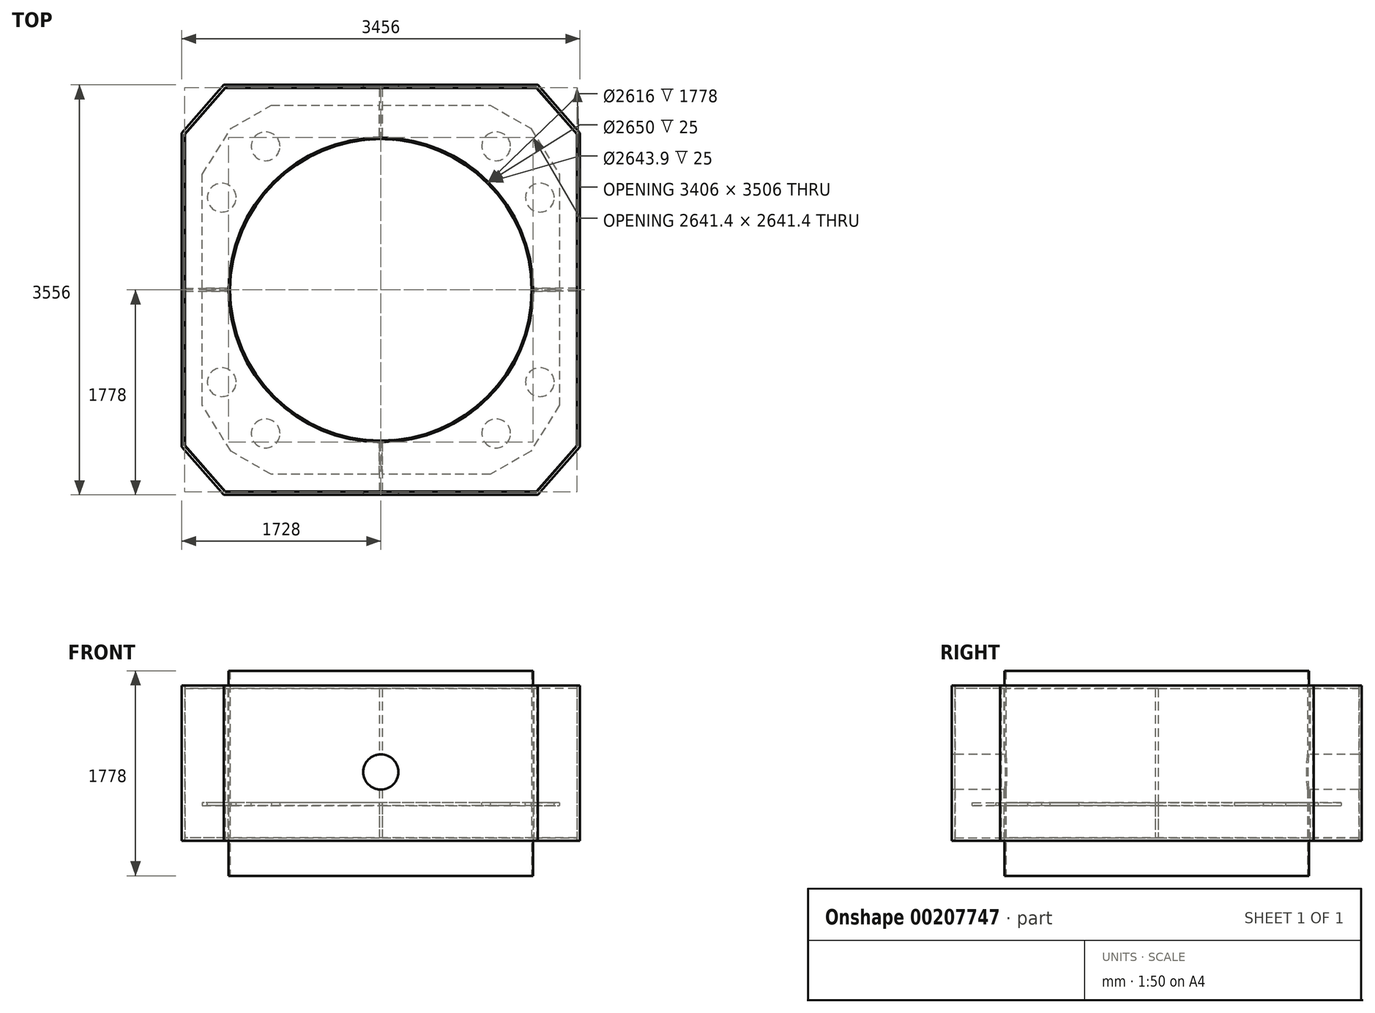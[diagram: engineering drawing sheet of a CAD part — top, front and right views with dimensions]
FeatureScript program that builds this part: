
annotation { "Feature Type Name" : "Feature", "Feature Type Description" : "" }
export const myFeature = defineFeature(function(context is Context, id is Id, definition is map)
    precondition{}
    {
        {
            var Q0;
            Q0=qCreatedBy(makeId("Front.planeOp"),FACE);
            var sketch = newSketch(context, id + "F0", { "sketchPlane" : qUnion([Q0])});
            skLineSegment(sketch, "E0", {"start": v(0, 0) * mm, "end": v(0, 90.62) * mm, "construction": true});
            skLineSegment(sketch, "E1.bottom", {"start": v(1308, 1778) * mm, "end": v(1320.7, 1778) * mm});
            skLineSegment(sketch, "E1.top", {"start": v(1308, 0) * mm, "end": v(1320.7, 0) * mm});
            skLineSegment(sketch, "E1.left", {"start": v(1308, 1778) * mm, "end": v(1308, 0) * mm});
            skLineSegment(sketch, "E1.right", {"start": v(1320.7, 1778) * mm, "end": v(1320.7, 0) * mm});
            skSolve(sketch);
        }
        {
            var Q0;
            Q0 = qSketchRegion(id + "F0", true);
            var Q1;
            Q1=sQuery(id+"F0.wireOp",EDGE,"E0");
            revolve(context, id + "F1", {"surfaceOperationType" : NewSurfaceOperationType.NEW, "entities" : qUnion([Q0]), "axis" : qUnion([Q1]), "revolveType" : RevolveType.FULL});
        }
        {
            var Q0;
            Q0=qCreatedBy(makeId("Top.planeOp"),FACE);
            cPlane(context, id + "F2", {"entities" : qUnion([Q0]), "cplaneType" : CPlaneType.OFFSET, "offset" : 304 * mm, "width" : 150 * mm, "height" : 150 * mm});
        }
        {
            var Q0;
            Q0=qCreatedBy(id+"F2.planeOp",FACE);
            var sketch = newSketch(context, id + "F3", { "sketchPlane" : qUnion([Q0])});
            skLineSegment(sketch, "E2.bottom", {"start": v(-1700, -1750) * mm, "end": v(1700, -1750) * mm});
            skLineSegment(sketch, "E2.top", {"start": v(-1700, 1750) * mm, "end": v(1700, 1750) * mm});
            skLineSegment(sketch, "E2.left", {"start": v(-1700, -1750) * mm, "end": v(-1700, 1750) * mm});
            skLineSegment(sketch, "E2.right", {"start": v(1700, -1750) * mm, "end": v(1700, 1750) * mm});
            skCircle(sketch, "E3", {"center": v(0, 0) * mm, "radius": 1325 * mm});
            skSolve(sketch);
        }
        {
            var Q0;
            Q0 = qSketchRegion(id + "F3", true);
            extrude(context, id + "F4", {"entities" : qUnion([Q0]), "depth" : 25 * mm, "offsetDistance" : 25 * mm});
        }
        {
            var Q0;
            Q0=qCreatedBy(id+"F2.planeOp",FACE);
            cPlane(context, id + "F5", {"entities" : qUnion([Q0]), "cplaneType" : CPlaneType.OFFSET, "offset" : 304 * mm, "width" : 150 * mm, "height" : 150 * mm});
        }
        {
            var Q0;
            Q0=qCreatedBy(id+"F5.planeOp",FACE);
            var sketch = newSketch(context, id + "F6", { "sketchPlane" : qUnion([Q0])});
            skCircle(sketch, "E4", {"center": v(0, 0) * mm, "radius": 1321.95 * mm});
            skLineSegment(sketch, "E5", {"start": v(-1300, -1400) * mm, "end": v(-1550, -1000) * mm});
            skLineSegment(sketch, "E6", {"start": v(-1550, -1000) * mm, "end": v(-1550, 1000) * mm});
            skLineSegment(sketch, "E7", {"start": v(-1550, 1000) * mm, "end": v(-1300, 1400) * mm});
            skLineSegment(sketch, "E8", {"start": v(1300, 1400) * mm, "end": v(1550, 1000) * mm});
            skLineSegment(sketch, "E9", {"start": v(1550, 1000) * mm, "end": v(1550, -1000) * mm});
            skLineSegment(sketch, "E10", {"start": v(1550, -1000) * mm, "end": v(1300, -1400) * mm});
            skLineSegment(sketch, "E11", {"start": v(-1300, 1400) * mm, "end": v(-950, 1600) * mm});
            skLineSegment(sketch, "E12", {"start": v(-950, 1600) * mm, "end": v(950, 1600) * mm});
            skLineSegment(sketch, "E13", {"start": v(950, 1600) * mm, "end": v(1300, 1400) * mm});
            skLineSegment(sketch, "E14", {"start": v(1300, -1400) * mm, "end": v(950, -1600) * mm});
            skLineSegment(sketch, "E15", {"start": v(950, -1600) * mm, "end": v(-950, -1600) * mm});
            skLineSegment(sketch, "E16", {"start": v(-950, -1600) * mm, "end": v(-1300, -1400) * mm});
            skSolve(sketch);
        }
        {
            var Q0;
            Q0 = qSketchRegion(id + "F6", true);
            extrude(context, id + "F7", {"entities" : qUnion([Q0]), "depth" : 25 * mm, "offsetDistance" : 25 * mm});
        }
        {
            var Q0;
            Q0=makeQuery(id+"F7.opExtrude","CAP_FACE",FACE,{"disambiguationData":[OSD([sQuery(id+"F6.wireOp",EDGE,"E4"),sQuery(id+"F6.wireOp",EDGE,"E5"),sQuery(id+"F6.wireOp",EDGE,"E6"),sQuery(id+"F6.wireOp",EDGE,"E7"),sQuery(id+"F6.wireOp",EDGE,"E8"),sQuery(id+"F6.wireOp",EDGE,"E9"),sQuery(id+"F6.wireOp",EDGE,"E10"),sQuery(id+"F6.wireOp",EDGE,"E11"),sQuery(id+"F6.wireOp",EDGE,"E12"),sQuery(id+"F6.wireOp",EDGE,"E13"),sQuery(id+"F6.wireOp",EDGE,"E14"),sQuery(id+"F6.wireOp",EDGE,"E15"),sQuery(id+"F6.wireOp",EDGE,"E16")])],"isStart":false});
            var sketch = newSketch(context, id + "F8", { "sketchPlane" : qUnion([Q0])});
            skCircle(sketch, "E17", {"center": v(-1380, 800) * mm, "radius": 125 * mm});
            skCircle(sketch, "E18", {"center": v(-1380, -800) * mm, "radius": 125 * mm});
            skCircle(sketch, "E19", {"center": v(1380, 800) * mm, "radius": 125 * mm});
            skCircle(sketch, "E20", {"center": v(1380, -800) * mm, "radius": 125 * mm});
            skCircle(sketch, "E21", {"center": v(-1000, 1245) * mm, "radius": 125 * mm});
            skCircle(sketch, "E22", {"center": v(1000, 1245) * mm, "radius": 125 * mm});
            skCircle(sketch, "E23", {"center": v(1000, -1245) * mm, "radius": 125 * mm});
            skCircle(sketch, "E24", {"center": v(-1000, -1245) * mm, "radius": 125 * mm});
            skSolve(sketch);
        }
        {
            var Q0;
            Q0 = qSketchRegion(id + "F8", true);
            extrude(context, id + "F9", {"entities" : qUnion([Q0]), "operationType" : NewBodyOperationType.REMOVE, "oppositeDirection" : true, "depth" : 25 * mm, "offsetDistance" : 25 * mm});
        }
        {
            var Q0;
            Q0=makeQuery(id+"F4.opExtrude","CAP_FACE",FACE,{"disambiguationData":[OSD([sQuery(id+"F3.wireOp",EDGE,"E2.bottom"),sQuery(id+"F3.wireOp",EDGE,"E2.top"),sQuery(id+"F3.wireOp",EDGE,"E2.left"),sQuery(id+"F3.wireOp",EDGE,"E2.right"),sQuery(id+"F3.wireOp",EDGE,"E3")])],"isStart":false});
            var sketch = newSketch(context, id + "F10", { "sketchPlane" : qUnion([Q0])});
            skLineSegment(sketch, "E25", {"start": v(1700, 1750) * mm, "end": v(1700, 1350) * mm});
            skLineSegment(sketch, "E26", {"start": v(1700, 1350) * mm, "end": v(1350, 1750) * mm});
            skLineSegment(sketch, "E27", {"start": v(1350, 1750) * mm, "end": v(1700, 1750) * mm});
            skLineSegment(sketch, "E28", {"start": v(1700, -1750) * mm, "end": v(1700, -1350) * mm});
            skLineSegment(sketch, "E29", {"start": v(1700, -1350) * mm, "end": v(1350, -1750) * mm});
            skLineSegment(sketch, "E30", {"start": v(1350, -1750) * mm, "end": v(1700, -1750) * mm});
            skLineSegment(sketch, "E31", {"start": v(-1350, -1750) * mm, "end": v(-1700, -1350) * mm});
            skLineSegment(sketch, "E32", {"start": v(-1700, -1750) * mm, "end": v(-1350, -1750) * mm});
            skLineSegment(sketch, "E33", {"start": v(-1350, 1750) * mm, "end": v(-1700, 1350) * mm});
            skLineSegment(sketch, "E34", {"start": v(-1700, 1750) * mm, "end": v(-1350, 1750) * mm});
            skLineSegment(sketch, "E35", {"start": v(-1700, 1750) * mm, "end": v(-1700, 1350) * mm});
            skLineSegment(sketch, "E36", {"start": v(-1700, -1350) * mm, "end": v(-1700, -1750) * mm});
            skSolve(sketch);
        }
        {
            var Q0;
            Q0 = qSketchRegion(id + "F10", true);
            extrude(context, id + "F11", {"entities" : qUnion([Q0]), "operationType" : NewBodyOperationType.REMOVE, "oppositeDirection" : true, "depth" : 25 * mm, "offsetDistance" : 25 * mm});
        }
        {
            var Q0;
            Q0=qCreatedBy(id+"F5.planeOp",FACE);
            cPlane(context, id + "F12", {"entities" : qUnion([Q0]), "cplaneType" : CPlaneType.OFFSET, "offset" : 1016 * mm, "width" : 150 * mm, "height" : 150 * mm});
        }
        {
            var Q0;
            Q0=qCreatedBy(id+"F12.planeOp",FACE);
            var sketch = newSketch(context, id + "F13", { "sketchPlane" : qUnion([Q0])});
            skLineSegment(sketch, "E37.0", {"start": v(-1350, 1750) * mm, "end": v(-1700, 1350) * mm});
            skLineSegment(sketch, "E38.0", {"start": v(-1700, -1350) * mm, "end": v(-1700, 1350) * mm});
            skLineSegment(sketch, "E39.0", {"start": v(-1350, -1750) * mm, "end": v(-1700, -1350) * mm});
            skLineSegment(sketch, "E40.0", {"start": v(-1350, -1750) * mm, "end": v(1350, -1750) * mm});
            skLineSegment(sketch, "E41.0", {"start": v(1700, -1350) * mm, "end": v(1350, -1750) * mm});
            skLineSegment(sketch, "E42.0", {"start": v(1700, -1350) * mm, "end": v(1700, 1350) * mm});
            skLineSegment(sketch, "E43.0", {"start": v(1700, 1350) * mm, "end": v(1350, 1750) * mm});
            skLineSegment(sketch, "E44.0", {"start": v(-1350, 1750) * mm, "end": v(1350, 1750) * mm});
            skCircle(sketch, "E45.0", {"center": v(0, 0) * mm, "radius": 1320.7 * mm});
            skSolve(sketch);
        }
        {
            var Q0;
            Q0 = qSketchRegion(id + "F13", true);
            extrude(context, id + "F14", {"entities" : qUnion([Q0]), "operationType" : NewBodyOperationType.ADD, "depth" : 25 * mm, "offsetDistance" : 25 * mm});
        }
        {
            var Q0;
            Q0=qCreatedBy(id+"F2.planeOp",FACE);
            var sketch = newSketch(context, id + "F15", { "sketchPlane" : qUnion([Q0])});
            skLineSegment(sketch, "E46.bottom", {"start": v(-12.7, 1750) * mm, "end": v(12.7, 1750) * mm});
            skLineSegment(sketch, "E46.top", {"start": v(-12.7, 1328.2) * mm, "end": v(12.7, 1328.2) * mm});
            skLineSegment(sketch, "E46.left", {"start": v(-12.7, 1750) * mm, "end": v(-12.7, 1328.2) * mm});
            skLineSegment(sketch, "E46.right", {"start": v(12.7, 1750) * mm, "end": v(12.7, 1328.2) * mm});
            skLineSegment(sketch, "E47.bottom", {"start": v(-12.7, -1328.2) * mm, "end": v(12.7, -1328.2) * mm});
            skLineSegment(sketch, "E47.top", {"start": v(-12.7, -1750) * mm, "end": v(12.7, -1750) * mm});
            skLineSegment(sketch, "E47.left", {"start": v(-12.7, -1328.2) * mm, "end": v(-12.7, -1750) * mm});
            skLineSegment(sketch, "E47.right", {"start": v(12.7, -1328.2) * mm, "end": v(12.7, -1750) * mm});
            skLineSegment(sketch, "E48.bottom", {"start": v(-1700, 12.7) * mm, "end": v(-1328.2, 12.7) * mm});
            skLineSegment(sketch, "E48.top", {"start": v(-1700, -12.7) * mm, "end": v(-1328.2, -12.7) * mm});
            skLineSegment(sketch, "E48.left", {"start": v(-1700, 12.7) * mm, "end": v(-1700, -12.7) * mm});
            skLineSegment(sketch, "E48.right", {"start": v(-1328.2, 12.7) * mm, "end": v(-1328.2, -12.7) * mm});
            skLineSegment(sketch, "E49.bottom", {"start": v(1700, 12.7) * mm, "end": v(1328.2, 12.7) * mm});
            skLineSegment(sketch, "E49.top", {"start": v(1700, -12.7) * mm, "end": v(1328.2, -12.7) * mm});
            skLineSegment(sketch, "E49.left", {"start": v(1700, 12.7) * mm, "end": v(1700, -12.7) * mm});
            skLineSegment(sketch, "E49.right", {"start": v(1328.2, 12.7) * mm, "end": v(1328.2, -12.7) * mm});
            skSolve(sketch);
        }
        {
            var Q0;
            Q0 = qSketchRegion(id + "F15", true);
            var Q1;
            Q1=makeQuery(id+"F14.opExtrude","CAP_FACE",FACE,{"disambiguationData":[OSD([sQuery(id+"F13.wireOp",EDGE,"E37.0"),sQuery(id+"F13.wireOp",EDGE,"E38.0"),sQuery(id+"F13.wireOp",EDGE,"E39.0"),sQuery(id+"F13.wireOp",EDGE,"E40.0"),sQuery(id+"F13.wireOp",EDGE,"E41.0"),sQuery(id+"F13.wireOp",EDGE,"E42.0"),sQuery(id+"F13.wireOp",EDGE,"E43.0"),sQuery(id+"F13.wireOp",EDGE,"E44.0"),sQuery(id+"F13.wireOp",EDGE,"E45.0")])],"isStart":true});
            extrude(context, id + "F16", {"entities" : qUnion([Q0]), "endBound" : BoundingType.UP_TO_SURFACE, "depth" : 25 * mm, "endBoundEntityFace" : qUnion([Q1]), "offsetDistance" : 25 * mm});
        }
        {
            var Q0;
            Q0=makeQuery(id+"F4.opExtrude","SWEPT_BODY",BODY,{"disambiguationData":[OSD([sQuery(id+"F3.wireOp",EDGE,"E2.bottom"),sQuery(id+"F3.wireOp",EDGE,"E2.top"),sQuery(id+"F3.wireOp",EDGE,"E2.left"),sQuery(id+"F3.wireOp",EDGE,"E2.right"),sQuery(id+"F3.wireOp",EDGE,"E3")])]});
            var Q1;
            Q1=makeQuery(id+"F7.opExtrude","SWEPT_BODY",BODY,{"disambiguationData":[OSD([sQuery(id+"F6.wireOp",EDGE,"E4"),sQuery(id+"F6.wireOp",EDGE,"E5"),sQuery(id+"F6.wireOp",EDGE,"E6"),sQuery(id+"F6.wireOp",EDGE,"E7"),sQuery(id+"F6.wireOp",EDGE,"E8"),sQuery(id+"F6.wireOp",EDGE,"E9"),sQuery(id+"F6.wireOp",EDGE,"E10"),sQuery(id+"F6.wireOp",EDGE,"E11"),sQuery(id+"F6.wireOp",EDGE,"E12"),sQuery(id+"F6.wireOp",EDGE,"E13"),sQuery(id+"F6.wireOp",EDGE,"E14"),sQuery(id+"F6.wireOp",EDGE,"E15"),sQuery(id+"F6.wireOp",EDGE,"E16")])]});
            var Q2;
            Q2=makeQuery(id+"F16.opExtrude","SWEPT_BODY",BODY,{"disambiguationData":[OSD([sQuery(id+"F15.wireOp",EDGE,"E46.bottom"),sQuery(id+"F15.wireOp",EDGE,"E46.top"),sQuery(id+"F15.wireOp",EDGE,"E46.left"),sQuery(id+"F15.wireOp",EDGE,"E46.right")])]});
            var Q3;
            Q3=makeQuery(id+"F16.opExtrude","SWEPT_BODY",BODY,{"disambiguationData":[OSD([sQuery(id+"F15.wireOp",EDGE,"E47.bottom"),sQuery(id+"F15.wireOp",EDGE,"E47.top"),sQuery(id+"F15.wireOp",EDGE,"E47.left"),sQuery(id+"F15.wireOp",EDGE,"E47.right")])]});
            var Q4;
            Q4=makeQuery(id+"F16.opExtrude","SWEPT_BODY",BODY,{"disambiguationData":[OSD([sQuery(id+"F15.wireOp",EDGE,"E49.bottom"),sQuery(id+"F15.wireOp",EDGE,"E49.top"),sQuery(id+"F15.wireOp",EDGE,"E49.left"),sQuery(id+"F15.wireOp",EDGE,"E49.right")])]});
            var Q5;
            Q5=makeQuery(id+"F16.opExtrude","SWEPT_BODY",BODY,{"disambiguationData":[OSD([sQuery(id+"F15.wireOp",EDGE,"E48.bottom"),sQuery(id+"F15.wireOp",EDGE,"E48.top"),sQuery(id+"F15.wireOp",EDGE,"E48.left"),sQuery(id+"F15.wireOp",EDGE,"E48.right")])]});
            booleanBodies(context, id + "F17", {"operationType" : BooleanOperationType.UNION, "tools" : qUnion([Q0, Q1, Q2, Q3, Q4, Q5])});
        }
        {
            var Q0;
            Q0=makeQuery(id+"F1.opRevolve","SWEPT_BODY",BODY,{"disambiguationData":[OSD([sQuery(id+"F0.wireOp",EDGE,"E1.bottom"),sQuery(id+"F0.wireOp",EDGE,"E1.top"),sQuery(id+"F0.wireOp",EDGE,"E1.left"),sQuery(id+"F0.wireOp",EDGE,"E1.right")])]});
            var Q1;
            Q1=makeQuery(id+"F4.opExtrude","SWEPT_BODY",BODY,{"disambiguationData":[OSD([sQuery(id+"F3.wireOp",EDGE,"E2.bottom"),sQuery(id+"F3.wireOp",EDGE,"E2.top"),sQuery(id+"F3.wireOp",EDGE,"E2.left"),sQuery(id+"F3.wireOp",EDGE,"E2.right"),sQuery(id+"F3.wireOp",EDGE,"E3")])]});
            booleanBodies(context, id + "F18", {"operationType" : BooleanOperationType.UNION, "tools" : qUnion([Q0, Q1])});
        }
        {
            var Q0;
            Q0=qCreatedBy(makeId("Front.planeOp"),FACE);
            var sketch = newSketch(context, id + "F19", { "sketchPlane" : qUnion([Q0])});
            skCircle(sketch, "E50", {"center": v(0, 900) * mm, "radius": 152.5 * mm});
            skSolve(sketch);
        }
        {
            var Q0;
            Q0=makeQuery(id+"F4.opExtrude","CAP_FACE",FACE,{"disambiguationData":[OSD([sQuery(id+"F3.wireOp",EDGE,"E2.bottom"),sQuery(id+"F3.wireOp",EDGE,"E2.top"),sQuery(id+"F3.wireOp",EDGE,"E2.left"),sQuery(id+"F3.wireOp",EDGE,"E2.right"),sQuery(id+"F3.wireOp",EDGE,"E3")])],"isStart":true});
            var sketch = newSketch(context, id + "F20", { "sketchPlane" : qUnion([Q0])});
            skLineSegment(sketch, "E51.0", {"start": v(-1351.36, -1753) * mm, "end": v(1351.36, -1753) * mm});
            skLineSegment(sketch, "E51.1", {"start": v(1703, -1351.13) * mm, "end": v(1351.36, -1753) * mm});
            skLineSegment(sketch, "E51.2", {"start": v(-1351.36, -1753) * mm, "end": v(-1703, -1351.13) * mm});
            skLineSegment(sketch, "E51.3", {"start": v(1703, 1351.13) * mm, "end": v(1703, -1351.13) * mm});
            skLineSegment(sketch, "E51.4", {"start": v(-1703, 1351.13) * mm, "end": v(-1703, -1351.13) * mm});
            skLineSegment(sketch, "E51.5", {"start": v(-1351.36, 1753) * mm, "end": v(-1703, 1351.13) * mm});
            skLineSegment(sketch, "E51.6", {"start": v(-1351.36, 1753) * mm, "end": v(1351.36, 1753) * mm});
            skLineSegment(sketch, "E51.7", {"start": v(1703, 1351.13) * mm, "end": v(1351.36, 1753) * mm});
            skLineSegment(sketch, "E52.0", {"start": v(-1362.7, -1778) * mm, "end": v(1362.7, -1778) * mm});
            skLineSegment(sketch, "E52.1", {"start": v(1728, -1360.52) * mm, "end": v(1362.7, -1778) * mm});
            skLineSegment(sketch, "E52.2", {"start": v(-1362.7, -1778) * mm, "end": v(-1728, -1360.52) * mm});
            skLineSegment(sketch, "E52.3", {"start": v(1728, 1360.52) * mm, "end": v(1728, -1360.52) * mm});
            skLineSegment(sketch, "E52.4", {"start": v(-1728, 1360.52) * mm, "end": v(-1728, -1360.52) * mm});
            skLineSegment(sketch, "E52.5", {"start": v(-1362.7, 1778) * mm, "end": v(-1728, 1360.52) * mm});
            skLineSegment(sketch, "E52.6", {"start": v(-1362.7, 1778) * mm, "end": v(1362.7, 1778) * mm});
            skLineSegment(sketch, "E52.7", {"start": v(1728, 1360.52) * mm, "end": v(1362.7, 1778) * mm});
            skSolve(sketch);
        }
        {
            var Q0;
            Q0 = qSketchRegion(id + "F20", true);
            var Q1;
            Q1=makeQuery(id+"F14.opExtrude","CAP_FACE",FACE,{"disambiguationData":[OSD([sQuery(id+"F13.wireOp",EDGE,"E37.0"),sQuery(id+"F13.wireOp",EDGE,"E38.0"),sQuery(id+"F13.wireOp",EDGE,"E39.0"),sQuery(id+"F13.wireOp",EDGE,"E40.0"),sQuery(id+"F13.wireOp",EDGE,"E41.0"),sQuery(id+"F13.wireOp",EDGE,"E42.0"),sQuery(id+"F13.wireOp",EDGE,"E43.0"),sQuery(id+"F13.wireOp",EDGE,"E44.0"),sQuery(id+"F13.wireOp",EDGE,"E45.0")])],"isStart":false});
            extrude(context, id + "F21", {"entities" : qUnion([Q0]), "endBound" : BoundingType.UP_TO_SURFACE, "oppositeDirection" : true, "depth" : 25 * mm, "endBoundEntityFace" : qUnion([Q1]), "offsetDistance" : 25 * mm});
        }
        {
            var Q0;
            Q0 = qSketchRegion(id + "F19", true);
            extrude(context, id + "F22", {"entities" : qUnion([Q0]), "operationType" : NewBodyOperationType.REMOVE, "endBound" : BoundingType.SYMMETRIC, "oppositeDirection" : true, "depth" : 8000 * mm, "offsetDistance" : 25 * mm});
        }
    });
